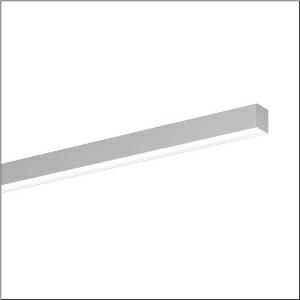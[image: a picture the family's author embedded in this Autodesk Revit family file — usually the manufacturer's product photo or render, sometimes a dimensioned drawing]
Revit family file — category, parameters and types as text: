
# Revit family: silica_21_51mx20da42sb
name_source: partatom
category: Lighting Fixtures
units: mm (PartAtom-declared; Revit-internal decimal feet)

## family parameters
Cut with Voids When Loaded = No
Host = Face
Light Source = No
Part Type = Normal
Room Calculation Point = No
Round Connector Dimension = Use Diameter
Shared = No

## types (1)
- --- (1 x LED, 2400 lm, 15.2 W, 4000K)
    Apparent Load = 15 VA
    CIE Flux Codes = 48 79 96 100 100
    Color Rendering = 80
    Color Temperature = 4000K
    Default Elevation = 1800 mm
    Description = Silica 21, office luminaire, primary optical cover: cover, of PMMA, opal, light emission: direct distribution, primary light characteristic: symmetric, installation type: surface-mounted, LED, rated luminous flux: 2.400lm, luminous efficacy: 158lm/W, light colour: 840, colour temperature: 4000K, control gear: DALI 2, with terminal, 3+2-pole, max. 2.5mm², mains connection: 220..240V, AC, 50/60Hz, rated input power: 15.2W, luminaire housing, of aluminium, metallic grey (RAL 9006), length: 1.204mm, width: 53mm, height: 53mm, protection rating (complete): IP20, insulation class (complete): insulation class I (protective earthing), certification: CE, permissible operating ambient temperature: 0..+35°C, standard: EN 50419, packaging unit: 1 piece
    Height = 53 mm
    Lamp = 1 x LED
    Lamp Light Flux = 2400 lm
    Lamp Power = 15.2 W
    Lamp count = 1
    Length = 1204 mm
    Luminous efficacy = 158 lm/W
    Manufacturer = Siteco
    ModVariant = No
    Model = 51MX20DA42SB
    Mounting Place = Ceiling
    Mounting Type = Surface mounted
    Number of Poles = 1
    OnlyDefault = Yes
    Power Factor = 1
    Product Name = Silica 21
    Product group = office luminaire | ceiling mounted
    ProductGroupID = 301
    Protection Class = Protection class I
    Protection Degree = IP 20
    RLX_Detail_Level = 1
    RLX_Emergency_Light_Flux = 0 lm
    RLX_Emergency_Type = 0
    RLX_Emergency_Type_DB = No
    RlxData = <blob elided: 26309 chars, md5=a9805c09>
    Socket = socket
    Standby Power = 0 W
    System Light Flux = 2400 lm
    System Power = 15 W
    Type Comments = factory setting: luminous flux: 100 % | dim-lin: 254 | 218 mA
    Type Image = l_1335933.jpg
    URL = http://relux.com
    VarID = @adj_027793
    Voltage = 0 V
    Weight = 0.00 kg
    Width = 53 mm

## geometry (parser evidence)
native form markers: Blend x4, Sweep x10
no freeform markers — native parametric forms only
